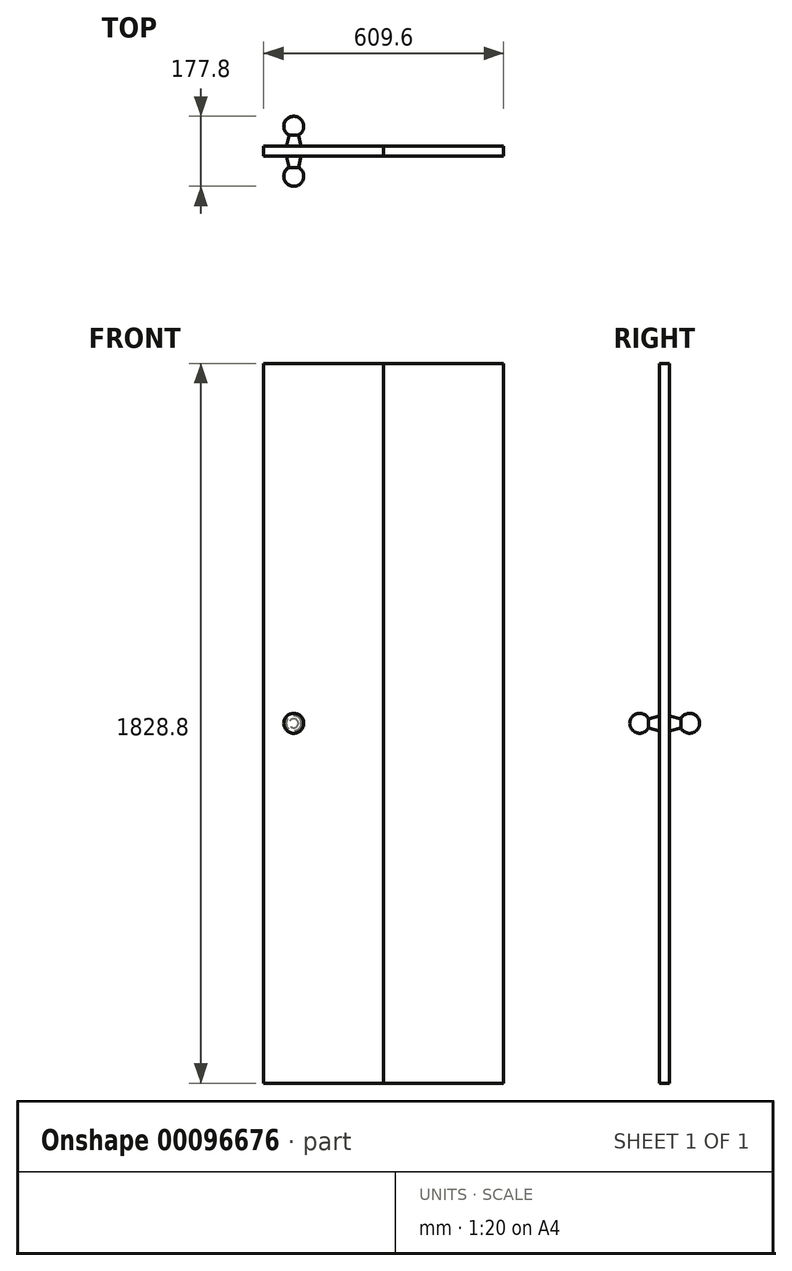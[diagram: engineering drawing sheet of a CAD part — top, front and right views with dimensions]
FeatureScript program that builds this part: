
annotation { "Feature Type Name" : "Feature", "Feature Type Description" : "" }
export const myFeature = defineFeature(function(context is Context, id is Id, definition is map)
    precondition{}
    {
        {
            var Q0;
            Q0=qCreatedBy(makeId("Front.planeOp"),FACE);
            var sketch = newSketch(context, id + "F0", { "sketchPlane" : qUnion([Q0])});
            skLineSegment(sketch, "E0.bottom", {"start": v(0, 0) * mm, "end": v(304.8, 0) * mm});
            skLineSegment(sketch, "E0.top", {"start": v(0, 1828.8) * mm, "end": v(304.8, 1828.8) * mm});
            skLineSegment(sketch, "E0.left", {"start": v(0, 0) * mm, "end": v(0, 1828.8) * mm});
            skLineSegment(sketch, "E0.right", {"start": v(304.8, 0) * mm, "end": v(304.8, 1828.8) * mm});
            skSolve(sketch);
        }
        {
            var Q0;
            Q0=qCreatedBy(makeId("Top.planeOp"),FACE);
            cPlane(context, id + "F1", {"entities" : qUnion([Q0]), "cplaneType" : CPlaneType.OFFSET, "offset" : 914.4 * mm, "width" : 152.4 * mm, "height" : 152.4 * mm});
        }
        {
            var Q0;
            Q0=qCreatedBy(id+"F1.planeOp",FACE);
            var sketch = newSketch(context, id + "F2", { "sketchPlane" : qUnion([Q0])});
            skArc(sketch, "E1", {"start": v(64.7, -28.16) * mm, "mid": v(51.5, -56.72) * mm, "end": v(76.2, -76.2) * mm});
            skLineSegment(sketch, "E2", {"start": v(57.15, 0) * mm, "end": v(76.2, 0) * mm});
            skLineSegment(sketch, "E3", {"start": v(57.15, 0) * mm, "end": v(64.7, -28.16) * mm});
            skLineSegment(sketch, "E4", {"start": v(76.2, 0) * mm, "end": v(76.2, -76.2) * mm});
            skSolve(sketch);
        }
        {
            var Q0;
            Q0=makeQuery(id+"F0.imprint","IMPRINT",FACE,{"disambiguationData":[TD([[makeQuery(id+"F0.imprint","IMPRINT",EDGE,{"derivedFrom":sQuery(id+"F0.wireOp",EDGE,"E0.bottom")}),1.0]])]});
            var sketch = newSketch(context, id + "F3", { "sketchPlane" : qUnion([Q0])});
            skCircle(sketch, "E5", {"center": v(76.2, 914.4) * mm, "radius": 34.7 * mm});
            skSolve(sketch);
        }
        {
            var Q0;
            Q0=makeQuery(id+"F0.imprint","IMPRINT",FACE,{"disambiguationData":[TD([[makeQuery(id+"F0.imprint","IMPRINT",EDGE,{"derivedFrom":sQuery(id+"F0.wireOp",EDGE,"E0.bottom")}),1.0]])]});
            extrude(context, id + "F4", {"entities" : qUnion([Q0]), "oppositeDirection" : true, "depth" : 25.4 * mm});
        }
        {
            var Q0;
            Q0=makeQuery(id+"F2.imprint","IMPRINT",FACE,{"disambiguationData":[TD([[makeQuery(id+"F2.imprint","IMPRINT",EDGE,{"derivedFrom":sQuery(id+"F2.wireOp",EDGE,"E1")}),1.0]])]});
            var Q1;
            Q1=sQuery(id+"F3.wireOp",EDGE,"E5");
            sweep(context, id + "F5", {"profiles" : qUnion([Q0]), "path" : qUnion([Q1])});
        }
        {
            var Q0;
            Q0=qCreatedBy(makeId("Front.planeOp"),FACE);
            cPlane(context, id + "F6", {"entities" : qUnion([Q0]), "cplaneType" : CPlaneType.OFFSET, "offset" : 12.7 * mm, "oppositeDirection" : true, "width" : 152.4 * mm, "height" : 152.4 * mm});
        }
        {
            var Q0;
            Q0=makeQuery(id+"F5.opSweep","SWEPT_BODY",BODY,{"disambiguationData":[OSD([sQuery(id+"F2.wireOp",EDGE,"E1"),sQuery(id+"F2.wireOp",EDGE,"E2"),sQuery(id+"F2.wireOp",EDGE,"E3"),sQuery(id+"F2.wireOp",EDGE,"E4"),sQuery(id+"F3.wireOp",EDGE,"E5")])]});
            var Q1;
            Q1=qCreatedBy(id+"F6.planeOp",FACE);
            mirror(context, id + "F7", {"operationType" : NewBodyOperationType.ADD, "entities" : qUnion([Q0]), "mirrorPlane" : qUnion([Q1])});
        }
        {
            var Q0;
            Q0=makeQuery(id+"F4.opExtrude","CAP_FACE",FACE,{"disambiguationData":[OSD([sQuery(id+"F0.wireOp",EDGE,"E0.bottom"),sQuery(id+"F0.wireOp",EDGE,"E0.top"),sQuery(id+"F0.wireOp",EDGE,"E0.left"),sQuery(id+"F0.wireOp",EDGE,"E0.right")])],"isStart":true});
            var sketch = newSketch(context, id + "F8", { "sketchPlane" : qUnion([Q0])});
            skLineSegment(sketch, "E6.bottom", {"start": v(304.8, 1828.8) * mm, "end": v(609.6, 1828.8) * mm});
            skLineSegment(sketch, "E6.top", {"start": v(304.8, 0) * mm, "end": v(609.6, 0) * mm});
            skLineSegment(sketch, "E6.left", {"start": v(304.8, 1828.8) * mm, "end": v(304.8, 0) * mm});
            skLineSegment(sketch, "E6.right", {"start": v(609.6, 1828.8) * mm, "end": v(609.6, 0) * mm});
            skSolve(sketch);
        }
        {
            var Q0;
            Q0=makeQuery(id+"F8.imprint","IMPRINT",FACE,{"disambiguationData":[TD([[makeQuery(id+"F8.imprint","IMPRINT",EDGE,{"derivedFrom":sQuery(id+"F8.wireOp",EDGE,"E6.bottom")}),-1.0]])]});
            extrude(context, id + "F9", {"entities" : qUnion([Q0]), "oppositeDirection" : true, "depth" : 25.4 * mm});
        }
    });
